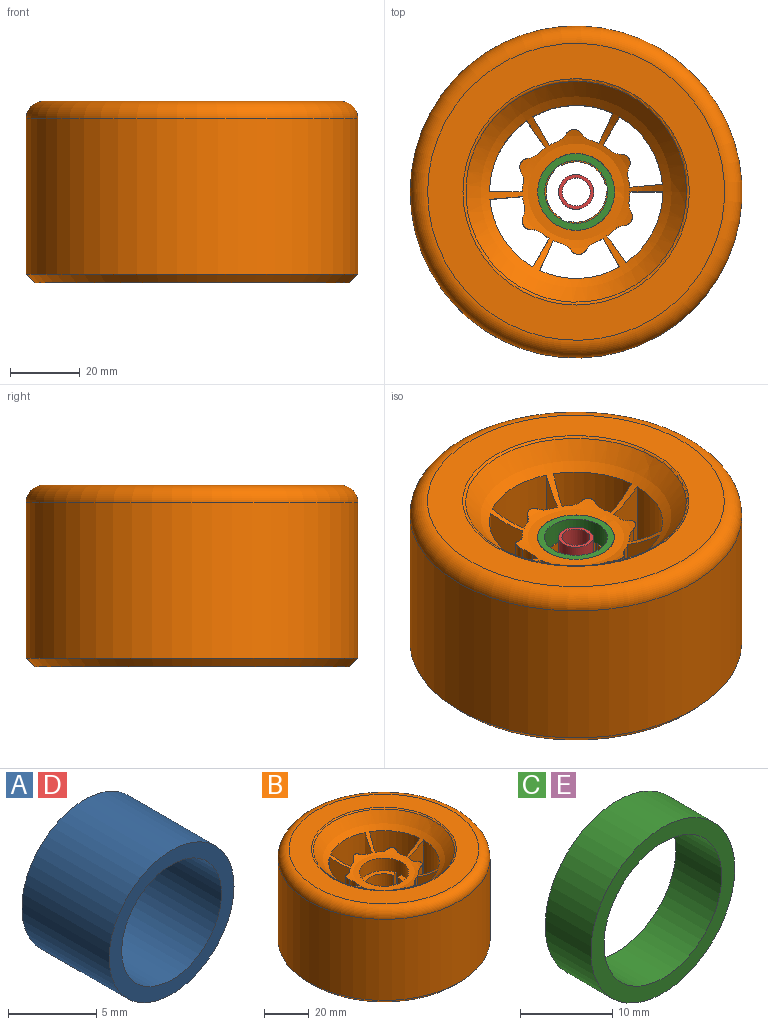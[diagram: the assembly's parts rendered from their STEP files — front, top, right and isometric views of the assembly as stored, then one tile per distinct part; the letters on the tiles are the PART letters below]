
ASSEMBLY  parts=5 mates=4
PART A: 4 faces, bbox 10x7x10 mm
  f0: cylinder r=4mm len=8mm, axis (0,1,0), area 175.9mm2, adj f2,f3
  f1: cylinder r=5mm len=10mm, axis (0,1,0), area 219.9mm2, adj f2,f3
  f2: plane 10x10mm, normal (0,-1,0), area 28.3mm2, adj f0,f1
  f3: plane 10x10mm, normal (0,1,0), area 28.3mm2, adj f0,f1
PART B: 73 faces, bbox 202x202x151.1 mm
  f0: cylinder r=8.64mm len=14.6mm, axis (0,0,-1), area 231.1mm2, adj f65,f66,f68,f72
  f1: cylinder r=8.64mm len=14.6mm, axis (0,0,-1), area 231.1mm2, adj f2,f4,f70,f71
  f2: plane 17.3x6.68mm, normal (0,0,1), area 42.5mm2, adj f1,f8,f70,f71
  f3: plane 16.13x8.77mm, normal (0,0,1), area 42.5mm2, adj f8,f64,f67,f69
  f4: plane 17.3x6.68mm, normal (0,0,-1), area 42.5mm2, adj f1,f8,f70,f71
  f5: plane 16.13x8.77mm, normal (0,0,-1), area 42.5mm2, adj f8,f64,f67,f69
  f6: revolved ~63.17x63.17mm, area 2298.8mm2, adj f8,f13,f14,f15,f16,f17,f18,f19
  f7: revolved ~61.35x61.35mm, area 3094.2mm2, adj f8,f11,f14,f15,f16,f17,f18,f19
  f8: cylinder r=11mm len=28.63mm, axis (0,0,1), area 1095.7mm2, adj f2,f3,f4,f5,f6,f7,f65,f66
  f9: plane 85x85mm, normal (0,0,1), area 2377.2mm2, adj f12,f13
  f10: cylinder r=47.5mm len=95mm, axis (0,0,1), area 13281.1mm2, adj f12,f63
  f11: plane 90x90mm, normal (0,0,-1), area 3405.5mm2, adj f7,f63
  f12: torus R=42.5mm, axis (0,0,-1), area 2254.4mm2, adj f9,f10
  f13: torus R=32.4mm, axis (0,0,1), area 190.7mm2, adj f6,f9
  f14: cylinder r=15.39mm len=29.22mm, axis (0,0,-1), area 73.3mm2, adj f6,f7,f15,f21
  f15: cylinder r=5mm len=29.88mm, axis (0,0,-1), area 102.1mm2, adj f6,f7,f14,f16
  f16: cylinder r=2.5mm len=30.47mm, axis (0,0,-1), area 153mm2, adj f6,f7,f15,f17
  f17: cylinder r=5mm len=29.88mm, axis (0,0,-1), area 102.1mm2, adj f6,f7,f16,f18
  f18: cylinder r=15.39mm len=29.22mm, axis (0,0,-1), area 73.3mm2, adj f6,f7,f17,f19
  f19: plane 36.96x8.14mm, normal (-0.87,-0.5,0), area 304.4mm2, adj f6,f7,f18,f20
  f20: cylinder r=24.79mm len=36.96mm, axis (0,0,-1), area 879.5mm2, adj f6,f7,f19,f21
  f21: plane 36.96x8.52mm, normal (0.91,-0.42,0), area 304.4mm2, adj f6,f7,f14,f20
  f22: cylinder r=2.5mm len=30.47mm, axis (0,0,-1), area 153mm2, adj f6,f7,f23,f30
  f23: cylinder r=5mm len=29.88mm, axis (0,0,-1), area 102.1mm2, adj f6,f7,f22,f24
  f24: cylinder r=15.39mm len=29.22mm, axis (0,0,-1), area 73.3mm2, adj f6,f7,f23,f25
  f25: plane 36.96x9.4mm, normal (0,-1,0), area 304.4mm2, adj f6,f7,f24,f26
  f26: cylinder r=24.79mm len=36.96mm, axis (0,0,-1), area 879.5mm2, adj f6,f7,f25,f28
  f27: cylinder r=24.79mm len=37.18mm, axis (0,0,-1), area 0mm2, adj f7
  f28: plane 136.11x106.84mm, normal (0.82,0.57,0), area 304.4mm2, adj f6,f7,f26,f29
  f29: cylinder r=15.39mm len=29.22mm, axis (0,0,-1), area 73.3mm2, adj f6,f7,f28,f30
  f30: cylinder r=5mm len=29.88mm, axis (0,0,-1), area 102.1mm2, adj f6,f7,f22,f29
  f31: cylinder r=2.5mm len=30.47mm, axis (0,0,-1), area 153mm2, adj f6,f7,f32,f38
  f32: cylinder r=5mm len=29.88mm, axis (0,0,-1), area 102.1mm2, adj f6,f7,f31,f33
  f33: cylinder r=15.39mm len=29.22mm, axis (0,0,-1), area 73.3mm2, adj f6,f7,f32,f34
  f34: plane 36.96x8.14mm, normal (-0.87,0.5,0), area 304.4mm2, adj f6,f7,f33,f35
  f35: cylinder r=24.79mm len=36.96mm, axis (0,0,-1), area 879.5mm2, adj f6,f7,f34,f36
  f36: plane 36.96x9.36mm, normal (0.09,-1,0), area 304.4mm2, adj f6,f7,f35,f37
  f37: cylinder r=15.39mm len=29.22mm, axis (0,0,-1), area 73.3mm2, adj f6,f7,f36,f38
  f38: cylinder r=5mm len=29.88mm, axis (0,0,-1), area 102.1mm2, adj f6,f7,f31,f37
  f39: cylinder r=2.5mm len=30.47mm, axis (0,0,-1), area 153mm2, adj f6,f7,f40,f46
  f40: cylinder r=5mm len=29.88mm, axis (0,0,-1), area 102.1mm2, adj f6,f7,f39,f41
  f41: cylinder r=15.39mm len=29.22mm, axis (0,0,-1), area 73.3mm2, adj f6,f7,f40,f42
  f42: plane 36.96x9.4mm, normal (0,1,0), area 304.4mm2, adj f6,f7,f41,f43
  f43: cylinder r=24.79mm len=36.96mm, axis (0,0,-1), area 879.5mm2, adj f6,f7,f42,f44
  f44: plane 36.96x7.7mm, normal (-0.82,-0.57,0), area 304.4mm2, adj f6,f7,f43,f45
  f45: cylinder r=15.39mm len=29.22mm, axis (0,0,-1), area 73.3mm2, adj f6,f7,f44,f46
  f46: cylinder r=5mm len=29.88mm, axis (0,0,-1), area 102.1mm2, adj f6,f7,f39,f45
  f47: cylinder r=2.5mm len=30.47mm, axis (0,0,-1), area 153mm2, adj f6,f7,f48,f54
  f48: cylinder r=5mm len=29.88mm, axis (0,0,-1), area 102.1mm2, adj f6,f7,f47,f49
  f49: cylinder r=15.39mm len=29.22mm, axis (0,0,-1), area 73.3mm2, adj f6,f7,f48,f50
  f50: plane 36.96x8.14mm, normal (0.87,-0.5,0), area 304.4mm2, adj f6,f7,f49,f51
  f51: cylinder r=24.79mm len=36.96mm, axis (0,0,-1), area 879.5mm2, adj f6,f7,f50,f52
  f52: plane 36.96x9.36mm, normal (-0.09,1,0), area 304.4mm2, adj f6,f7,f51,f53
  f53: cylinder r=15.39mm len=29.22mm, axis (0,0,-1), area 73.3mm2, adj f6,f7,f52,f54
  f54: cylinder r=5mm len=29.88mm, axis (0,0,-1), area 102.1mm2, adj f6,f7,f47,f53
  f55: cylinder r=2.5mm len=30.47mm, axis (0,0,-1), area 153mm2, adj f6,f7,f56,f62
  f56: cylinder r=5mm len=29.88mm, axis (0,0,-1), area 102.1mm2, adj f6,f7,f55,f57
  f57: cylinder r=15.39mm len=29.22mm, axis (0,0,-1), area 73.3mm2, adj f6,f7,f56,f58
  f58: plane 36.96x8.14mm, normal (0.87,0.5,0), area 304.4mm2, adj f6,f7,f57,f59
  f59: cylinder r=24.79mm len=36.96mm, axis (0,0,-1), area 879.5mm2, adj f6,f7,f58,f60
  f60: plane 36.96x8.52mm, normal (-0.91,0.42,0), area 304.4mm2, adj f6,f7,f59,f61
  f61: cylinder r=15.39mm len=29.22mm, axis (0,0,-1), area 73.3mm2, adj f6,f7,f60,f62
  f62: cylinder r=5mm len=29.88mm, axis (0,0,-1), area 102.1mm2, adj f6,f7,f55,f61
  f63: cone r=47.5mm half-angle=45deg, axis (0,0,1), area 1027.4mm2, adj f10,f11
  f64: cylinder r=8.64mm len=14.6mm, axis (0,0,-1), area 231.1mm2, adj f3,f5,f67,f69
  f65: plane 13.85x11mm, normal (0,0,1), area 42.5mm2, adj f0,f8,f68,f72
  f66: plane 13.85x11mm, normal (0,0,-1), area 42.5mm2, adj f0,f8,f68,f72
  f67: plane 14.6x2.28mm, normal (0.26,-0.97,0), area 34.5mm2, adj f3,f5,f8,f64
  f68: plane 14.6x2.36mm, normal (0,1,0), area 34.5mm2, adj f0,f8,f65,f66
  f69: plane 14.6x2.05mm, normal (-0.87,-0.5,0), area 34.5mm2, adj f3,f5,f8,f64
  f70: plane 14.6x1.67mm, normal (0.71,0.71,0), area 34.5mm2, adj f1,f2,f4,f8
  f71: plane 14.6x2.05mm, normal (0.87,-0.5,0), area 34.5mm2, adj f1,f2,f4,f8
  f72: plane 14.6x2.28mm, normal (-0.97,0.26,0), area 34.5mm2, adj f0,f8,f65,f66
PART C: 4 faces, bbox 22x7x22 mm
  f0: cylinder r=9mm len=18mm, axis (0,1,0), area 395.8mm2, adj f2,f3
  f1: cylinder r=11mm len=22mm, axis (0,1,0), area 483.8mm2, adj f2,f3
  f2: plane 22x22mm, normal (0,-1,0), area 125.7mm2, adj f0,f1
  f3: plane 22x22mm, normal (0,1,0), area 125.7mm2, adj f0,f1
PART D: same geometry as A
PART E: same geometry as C
PLACE A rot(axis=(-1,0,0),90deg) t=(27.3,0,-33.53)mm
PLACE B at identity
PLACE C rot(axis=(0.58,-0.58,-0.58),120deg) t=(27.3,0,-4.93)mm
PLACE D rot(axis=(1,0,0),90deg) t=(27.3,0,-4.93)mm
PLACE E rot(axis=(-1,0,0),90deg) t=(27.3,0,-33.53)mm
MATE fastened E.f0 <-> B.f0  axis (0,0,1) through (27.3,0,-26.53)mm
MATE revolute C.f0 <-> D.f0  axis (0,0,-1) through (27.3,0,-11.93)mm
MATE revolute A.f0 <-> E.f0  axis (0,0,-1) through (27.3,0,-26.53)mm
MATE fastened C.f0 <-> B.f0  axis (0,0,-1) through (27.3,0,-11.93)mm
